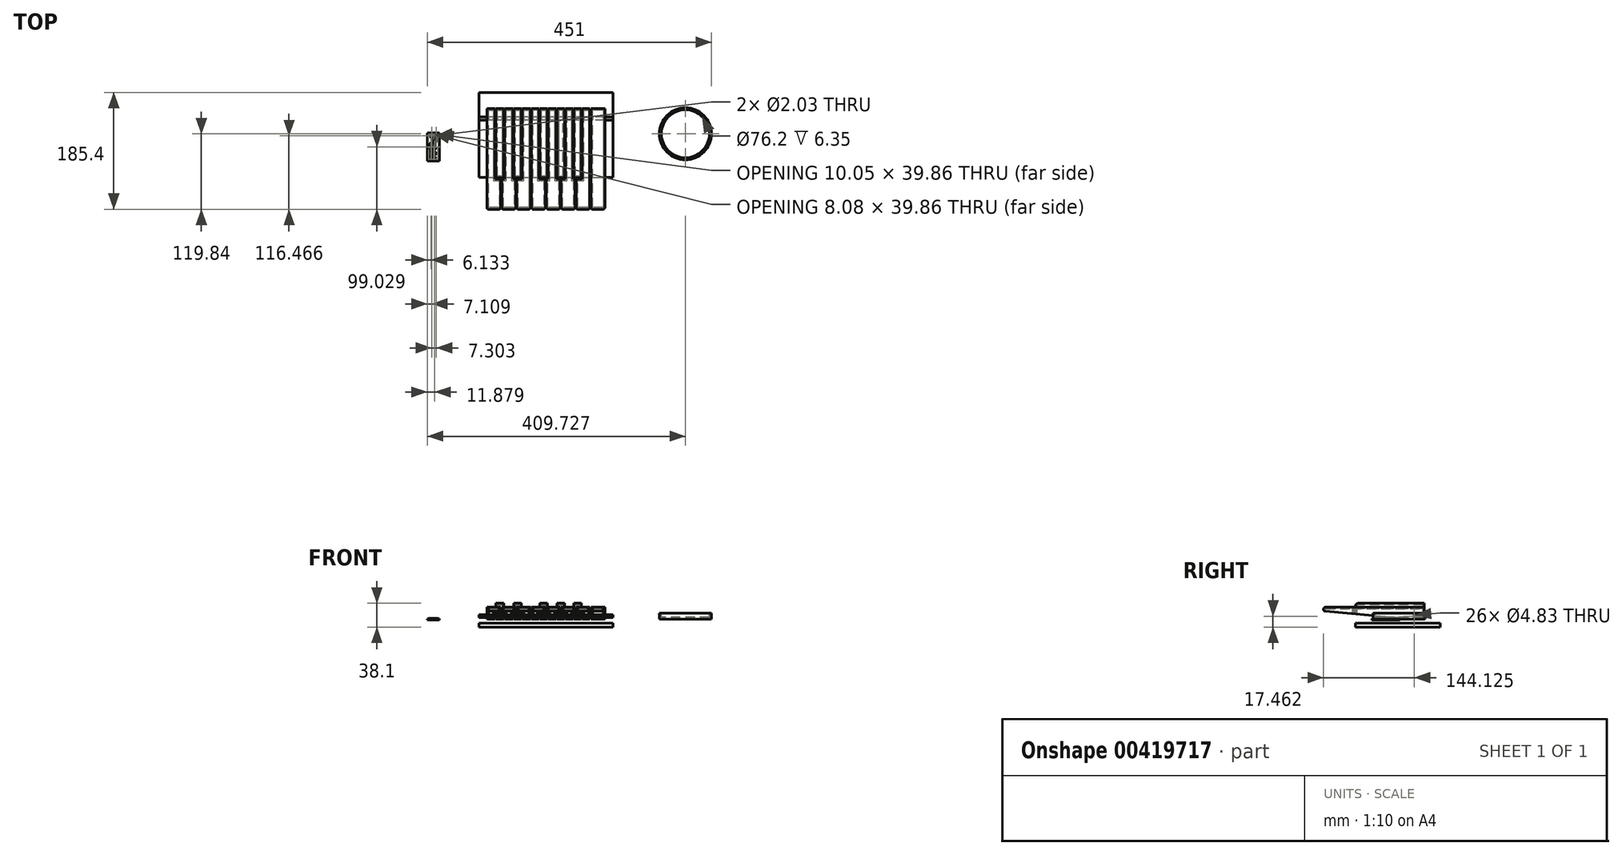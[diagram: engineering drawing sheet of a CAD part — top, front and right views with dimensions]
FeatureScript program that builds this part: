
annotation { "Feature Type Name" : "Feature", "Feature Type Description" : "" }
export const myFeature = defineFeature(function(context is Context, id is Id, definition is map)
    precondition{}
    {
        {
            var Q0;
            Q0=qCreatedBy(makeId("Top.planeOp"),FACE);
            var sketch = newSketch(context, id + "F0", { "sketchPlane" : qUnion([Q0])});
            skLineSegment(sketch, "E0", {"start": v(-10.7, 80) * mm, "end": v(-10.7, -32) * mm});
            skLineSegment(sketch, "E1", {"start": v(-10.7, -32) * mm, "end": v(-0.7, -32) * mm});
            skLineSegment(sketch, "E2", {"start": v(-0.7, -32) * mm, "end": v(-0.7, -80) * mm});
            skLineSegment(sketch, "E3", {"start": v(-0.7, -80) * mm, "end": v(-22.9, -80) * mm});
            skLineSegment(sketch, "E4", {"start": v(-22.9, -80) * mm, "end": v(-22.9, 80) * mm});
            skLineSegment(sketch, "E5", {"start": v(-24.3, 80) * mm, "end": v(-24.3, -80) * mm});
            skLineSegment(sketch, "E6", {"start": v(-24.3, -80) * mm, "end": v(-46.5, -80) * mm});
            skLineSegment(sketch, "E7", {"start": v(-46.5, -80) * mm, "end": v(-46.5, -32) * mm});
            skLineSegment(sketch, "E8", {"start": v(-46.5, -32) * mm, "end": v(-37.5, -32) * mm});
            skLineSegment(sketch, "E9", {"start": v(-37.5, -32) * mm, "end": v(-37.5, 80) * mm});
            skLineSegment(sketch, "E10", {"start": v(-37.5, 80) * mm, "end": v(-24.3, 80) * mm});
            skLineSegment(sketch, "E11", {"start": v(-38.85, 80) * mm, "end": v(-38.85, -30) * mm, "construction": true});
            skLineSegment(sketch, "E12", {"start": v(-38.85, -30) * mm, "end": v(-51.05, -30) * mm, "construction": true});
            skLineSegment(sketch, "E13", {"start": v(-51.05, -30) * mm, "end": v(-51.05, 80) * mm, "construction": true});
            skLineSegment(sketch, "E14", {"start": v(-51.05, 80) * mm, "end": v(-38.85, 80) * mm, "construction": true});
            skLineSegment(sketch, "E15", {"start": v(-52.4, 80) * mm, "end": v(-52.4, -32) * mm});
            skLineSegment(sketch, "E16", {"start": v(-52.4, -32) * mm, "end": v(-47.9, -32) * mm});
            skLineSegment(sketch, "E17", {"start": v(-47.9, -32) * mm, "end": v(-47.9, -80) * mm});
            skLineSegment(sketch, "E18", {"start": v(-47.9, -80) * mm, "end": v(-70.1, -80) * mm});
            skLineSegment(sketch, "E19", {"start": v(-70.1, -80) * mm, "end": v(-70.1, -32) * mm});
            skLineSegment(sketch, "E20", {"start": v(-70.1, -32) * mm, "end": v(-65.6, -32) * mm});
            skLineSegment(sketch, "E21", {"start": v(-65.6, -32) * mm, "end": v(-65.6, 80) * mm});
            skLineSegment(sketch, "E22", {"start": v(-65.6, 80) * mm, "end": v(-52.4, 80) * mm});
            skLineSegment(sketch, "E23", {"start": v(-66.95, 80) * mm, "end": v(-66.95, -30) * mm, "construction": true});
            skLineSegment(sketch, "E24", {"start": v(-66.95, -30) * mm, "end": v(-79.15, -30) * mm, "construction": true});
            skLineSegment(sketch, "E25", {"start": v(-79.15, -30) * mm, "end": v(-79.15, 80) * mm, "construction": true});
            skLineSegment(sketch, "E26", {"start": v(-79.15, 80) * mm, "end": v(-66.95, 80) * mm, "construction": true});
            skLineSegment(sketch, "E27", {"start": v(-80.5, 80) * mm, "end": v(-80.5, -32) * mm});
            skLineSegment(sketch, "E28", {"start": v(-80.5, -32) * mm, "end": v(-71.5, -32) * mm});
            skLineSegment(sketch, "E29", {"start": v(-71.5, -32) * mm, "end": v(-71.5, -80) * mm});
            skLineSegment(sketch, "E30", {"start": v(-71.5, -80) * mm, "end": v(-93.7, -80) * mm});
            skLineSegment(sketch, "E31", {"start": v(-93.7, -80) * mm, "end": v(-93.7, 80) * mm});
            skLineSegment(sketch, "E32", {"start": v(-93.7, 80) * mm, "end": v(-80.5, 80) * mm});
            skLineSegment(sketch, "E33", {"start": v(-9.43, 80) * mm, "end": v(2.77, 80) * mm, "construction": true});
            skLineSegment(sketch, "E34", {"start": v(2.77, 80) * mm, "end": v(2.77, -30) * mm, "construction": true});
            skLineSegment(sketch, "E35", {"start": v(2.77, -30) * mm, "end": v(-9.43, -30) * mm, "construction": true});
            skLineSegment(sketch, "E36", {"start": v(-9.43, -30) * mm, "end": v(-9.43, 80) * mm, "construction": true});
            skLineSegment(sketch, "E37", {"start": v(0.7, -80) * mm, "end": v(0.7, -32) * mm});
            skLineSegment(sketch, "E38", {"start": v(0.7, -32) * mm, "end": v(4.04, -32) * mm});
            skLineSegment(sketch, "E39", {"start": v(4.04, -32) * mm, "end": v(4.04, 80) * mm});
            skLineSegment(sketch, "E40", {"start": v(4.04, 80) * mm, "end": v(16.24, 80) * mm});
            skLineSegment(sketch, "E41", {"start": v(16.24, 80) * mm, "end": v(16.24, -32) * mm});
            skLineSegment(sketch, "E42", {"start": v(16.24, -32) * mm, "end": v(22.9, -32) * mm});
            skLineSegment(sketch, "E43", {"start": v(22.9, -32) * mm, "end": v(22.9, -80) * mm});
            skLineSegment(sketch, "E44", {"start": v(22.9, -80) * mm, "end": v(0.7, -80) * mm});
            skLineSegment(sketch, "E45", {"start": v(24.3, -80) * mm, "end": v(24.3, -32) * mm});
            skLineSegment(sketch, "E46", {"start": v(24.3, -32) * mm, "end": v(30.98, -32) * mm});
            skLineSegment(sketch, "E47", {"start": v(30.98, -32) * mm, "end": v(30.98, 80) * mm});
            skLineSegment(sketch, "E48", {"start": v(30.98, 80) * mm, "end": v(43.18, 80) * mm});
            skLineSegment(sketch, "E49", {"start": v(43.18, 80) * mm, "end": v(43.18, -32) * mm});
            skLineSegment(sketch, "E50", {"start": v(43.18, -32) * mm, "end": v(46.5, -32) * mm});
            skLineSegment(sketch, "E51", {"start": v(46.5, -32) * mm, "end": v(46.5, -80) * mm});
            skLineSegment(sketch, "E52", {"start": v(46.5, -80) * mm, "end": v(24.3, -80) * mm});
            skLineSegment(sketch, "E53", {"start": v(29.7, -30) * mm, "end": v(29.7, 80) * mm, "construction": true});
            skLineSegment(sketch, "E54", {"start": v(29.7, 80) * mm, "end": v(17.5, 80) * mm, "construction": true});
            skLineSegment(sketch, "E55", {"start": v(17.5, 80) * mm, "end": v(17.5, -30) * mm, "construction": true});
            skLineSegment(sketch, "E56", {"start": v(17.5, -30) * mm, "end": v(29.7, -30) * mm, "construction": true});
            skLineSegment(sketch, "E57", {"start": v(70.12, 80) * mm, "end": v(70.12, -80) * mm});
            skLineSegment(sketch, "E58", {"start": v(70.12, -80) * mm, "end": v(47.92, -80) * mm});
            skLineSegment(sketch, "E59", {"start": v(47.92, -80) * mm, "end": v(47.92, -32) * mm});
            skLineSegment(sketch, "E60", {"start": v(47.92, -32) * mm, "end": v(57.92, -32) * mm});
            skLineSegment(sketch, "E61", {"start": v(57.92, -32) * mm, "end": v(57.92, 80) * mm});
            skLineSegment(sketch, "E62", {"start": v(57.92, 80) * mm, "end": v(70.12, 80) * mm});
            skLineSegment(sketch, "E63", {"start": v(56.65, 80) * mm, "end": v(56.65, -30) * mm, "construction": true});
            skLineSegment(sketch, "E64", {"start": v(56.65, -30) * mm, "end": v(44.45, -30) * mm, "construction": true});
            skLineSegment(sketch, "E65", {"start": v(44.45, -30) * mm, "end": v(44.45, 80) * mm, "construction": true});
            skLineSegment(sketch, "E66", {"start": v(44.45, 80) * mm, "end": v(56.65, 80) * mm, "construction": true});
            skLineSegment(sketch, "E67", {"start": v(93.7, 80) * mm, "end": v(93.7, -80) * mm});
            skLineSegment(sketch, "E68", {"start": v(93.7, -80) * mm, "end": v(71.5, -80) * mm});
            skLineSegment(sketch, "E69", {"start": v(71.5, -80) * mm, "end": v(71.5, 80) * mm});
            skLineSegment(sketch, "E70", {"start": v(93.7, 80) * mm, "end": v(71.5, 80) * mm});
            skLineSegment(sketch, "E71", {"start": v(-10.7, 80) * mm, "end": v(-22.9, 80) * mm});
            skSolve(sketch);
        }
        {
            var Q0;
            Q0 = qSketchRegion(id + "F0", true);
            extrude(context, id + "F1", {"entities" : qUnion([Q0]), "depth" : 19.05 * mm});
        }
        {
            var Q0;
            Q0=qCreatedBy(makeId("Top.planeOp"),FACE);
            var sketch = newSketch(context, id + "F2", { "sketchPlane" : qUnion([Q0])});
            skLineSegment(sketch, "E72.13", {"start": v(-38.85, 80) * mm, "end": v(-38.85, -30) * mm});
            skLineSegment(sketch, "E72.14", {"start": v(-38.85, -30) * mm, "end": v(-51.05, -30) * mm});
            skLineSegment(sketch, "E72.15", {"start": v(-51.05, -30) * mm, "end": v(-51.05, 80) * mm});
            skLineSegment(sketch, "E72.16", {"start": v(-51.05, 80) * mm, "end": v(-38.85, 80) * mm});
            skLineSegment(sketch, "E72.25", {"start": v(-66.95, 80) * mm, "end": v(-66.95, -30) * mm});
            skLineSegment(sketch, "E72.26", {"start": v(-66.95, -30) * mm, "end": v(-79.15, -30) * mm});
            skLineSegment(sketch, "E72.27", {"start": v(-79.15, -30) * mm, "end": v(-79.15, 80) * mm});
            skLineSegment(sketch, "E72.28", {"start": v(-79.15, 80) * mm, "end": v(-66.95, 80) * mm});
            skLineSegment(sketch, "E72.35", {"start": v(-9.43, 80) * mm, "end": v(2.77, 80) * mm});
            skLineSegment(sketch, "E72.36", {"start": v(2.77, 80) * mm, "end": v(2.77, -30) * mm});
            skLineSegment(sketch, "E72.37", {"start": v(2.77, -30) * mm, "end": v(-9.43, -30) * mm});
            skLineSegment(sketch, "E72.38", {"start": v(-9.43, -30) * mm, "end": v(-9.43, 80) * mm});
            skLineSegment(sketch, "E72.55", {"start": v(29.7, -30) * mm, "end": v(29.7, 80) * mm});
            skLineSegment(sketch, "E72.56", {"start": v(29.7, 80) * mm, "end": v(17.5, 80) * mm});
            skLineSegment(sketch, "E72.57", {"start": v(17.5, 80) * mm, "end": v(17.5, -30) * mm});
            skLineSegment(sketch, "E72.58", {"start": v(17.5, -30) * mm, "end": v(29.7, -30) * mm});
            skLineSegment(sketch, "E72.65", {"start": v(56.65, 80) * mm, "end": v(56.65, -30) * mm});
            skLineSegment(sketch, "E72.66", {"start": v(56.65, -30) * mm, "end": v(44.45, -30) * mm});
            skLineSegment(sketch, "E72.67", {"start": v(44.45, -30) * mm, "end": v(44.45, 80) * mm});
            skLineSegment(sketch, "E72.68", {"start": v(44.45, 80) * mm, "end": v(56.65, 80) * mm});
            skPoint(sketch, "E72.29.end.orphan", {"position": v(-80.5, -32) * mm});
            skSolve(sketch);
        }
        {
            var Q0;
            Q0 = qSketchRegion(id + "F2", true);
            extrude(context, id + "F3", {"entities" : qUnion([Q0]), "depth" : 25.4 * mm});
        }
        {
            var Q0;
            Q0=makeQuery(id+"F1.opExtrude","SWEPT_FACE",FACE,{"disambiguationData":[OSD([sQuery(id+"F0.wireOp",EDGE,"E31")])]});
            var sketch = newSketch(context, id + "F4", { "sketchPlane" : qUnion([Q0])});
            skCircle(sketch, "E73", {"center": v(-64.12, 4.76) * mm, "radius": 2.41 * mm});
            skSolve(sketch);
        }
        {
            var Q0;
            Q0=makeQuery(id+"F1.opExtrude","SWEPT_FACE",FACE,{"disambiguationData":[OSD([sQuery(id+"F0.wireOp",EDGE,"E31")])]});
            var sketch = newSketch(context, id + "F5", { "sketchPlane" : qUnion([Q0])});
            skLineSegment(sketch, "E74", {"start": v(80, 0) * mm, "end": v(80, 12.7) * mm});
            skCircle(sketch, "E75.0", {"center": v(-64.12, 4.76) * mm, "radius": 2.41 * mm, "construction": true});
            skPoint(sketch, "E76", {"position": v(-64.12, 0) * mm});
            skLineSegment(sketch, "E77", {"start": v(80, 12.7) * mm, "end": v(-64.12, 0) * mm});
            skLineSegment(sketch, "E78", {"start": v(-64.12, 0) * mm, "end": v(80, 0) * mm});
            skSolve(sketch);
        }
        {
            var Q0;
            Q0 = qSketchRegion(id + "F5", true);
            var Q1;
            Q1=makeQuery(id+"F1.opExtrude","SWEPT_FACE",FACE,{"disambiguationData":[OSD([sQuery(id+"F0.wireOp",EDGE,"E67")])]});
            extrude(context, id + "F6", {"entities" : qUnion([Q0]), "operationType" : NewBodyOperationType.REMOVE, "endBound" : BoundingType.THROUGH_ALL, "oppositeDirection" : true, "endBoundEntityFace" : qUnion([Q1]), "depth" : 25.4 * mm});
        }
        {
            var Q0;
            Q0=makeQuery(id+"F1.opExtrude","SWEPT_FACE",FACE,{"disambiguationData":[OSD([sQuery(id+"F0.wireOp",EDGE,"E30")])]});
            var Q1;
            Q1=makeQuery(id+"F1.opExtrude","SWEPT_FACE",FACE,{"disambiguationData":[OSD([sQuery(id+"F0.wireOp",EDGE,"E18")])]});
            var Q2;
            Q2=makeQuery(id+"F1.opExtrude","SWEPT_FACE",FACE,{"disambiguationData":[OSD([sQuery(id+"F0.wireOp",EDGE,"E6")])]});
            var Q3;
            Q3=makeQuery(id+"F1.opExtrude","SWEPT_FACE",FACE,{"disambiguationData":[OSD([sQuery(id+"F0.wireOp",EDGE,"E3")])]});
            var Q4;
            Q4=makeQuery(id+"F1.opExtrude","SWEPT_FACE",FACE,{"disambiguationData":[OSD([sQuery(id+"F0.wireOp",EDGE,"E44")])]});
            var Q5;
            Q5=makeQuery(id+"F1.opExtrude","SWEPT_FACE",FACE,{"disambiguationData":[OSD([sQuery(id+"F0.wireOp",EDGE,"E52")])]});
            var Q6;
            Q6=makeQuery(id+"F1.opExtrude","SWEPT_FACE",FACE,{"disambiguationData":[OSD([sQuery(id+"F0.wireOp",EDGE,"E58")])]});
            var Q7;
            Q7=makeQuery(id+"F1.opExtrude","SWEPT_FACE",FACE,{"disambiguationData":[OSD([sQuery(id+"F0.wireOp",EDGE,"E68")])]});
            fillet(context, id + "F7", {"entities" : qUnion([Q0, Q1, Q2, Q3, Q4, Q5, Q6, Q7]), "radius" : 3.17 * mm, "tangentPropagation" : true, "allowEdgeOverflow" : false});
        }
        {
            var Q0;
            Q0=makeQuery(id+"F1.opExtrude","CAP_FACE",FACE,{"disambiguationData":[OSD([sQuery(id+"F0.wireOp",EDGE,"E27"),sQuery(id+"F0.wireOp",EDGE,"E28"),sQuery(id+"F0.wireOp",EDGE,"E29"),sQuery(id+"F0.wireOp",EDGE,"E30"),sQuery(id+"F0.wireOp",EDGE,"E31"),sQuery(id+"F0.wireOp",EDGE,"E32")])],"isStart":true});
            var Q1;
            {var subQ4=sQuery(id+"F0.wireOp",EDGE,"E27");Q1=makeQuery(id+"F6.boolean.opBoolean","COPY",FACE,{"disambiguationData":[TD([makeQuery(id+"F1.opExtrude","SWEPT_FACE",FACE,{"disambiguationData":[OSD([subQ4])]})])],"derivedFrom":makeQuery(id+"F6.opExtrude","SWEPT_FACE",FACE,{"disambiguationData":[OSD([sQuery(id+"F5.wireOp",EDGE,"E77")])]})});}
            var Q2;
            {var subQ0=sQuery(id+"F2.wireOp",EDGE,"E72.25");Q2=makeQuery(id+"F6.boolean.opBoolean","COPY",FACE,{"disambiguationData":[TD([makeQuery(id+"F3.opExtrude","SWEPT_FACE",FACE,{"disambiguationData":[OSD([subQ0])]})])],"derivedFrom":makeQuery(id+"F6.opExtrude","SWEPT_FACE",FACE,{"disambiguationData":[OSD([sQuery(id+"F5.wireOp",EDGE,"E77")])]})});}
            var Q3;
            {var subQ6=sQuery(id+"F0.wireOp",EDGE,"E15");Q3=makeQuery(id+"F6.boolean.opBoolean","COPY",FACE,{"disambiguationData":[TD([makeQuery(id+"F1.opExtrude","SWEPT_FACE",FACE,{"disambiguationData":[OSD([subQ6])]})])],"derivedFrom":makeQuery(id+"F6.opExtrude","SWEPT_FACE",FACE,{"disambiguationData":[OSD([sQuery(id+"F5.wireOp",EDGE,"E77")])]})});}
            var Q4;
            {var subQ0=sQuery(id+"F2.wireOp",EDGE,"E72.13");Q4=makeQuery(id+"F6.boolean.opBoolean","COPY",FACE,{"disambiguationData":[TD([makeQuery(id+"F3.opExtrude","SWEPT_FACE",FACE,{"disambiguationData":[OSD([subQ0])]})])],"derivedFrom":makeQuery(id+"F6.opExtrude","SWEPT_FACE",FACE,{"disambiguationData":[OSD([sQuery(id+"F5.wireOp",EDGE,"E77")])]})});}
            var Q5;
            {var subQ4=sQuery(id+"F0.wireOp",EDGE,"E5");Q5=makeQuery(id+"F6.boolean.opBoolean","COPY",FACE,{"disambiguationData":[TD([makeQuery(id+"F1.opExtrude","SWEPT_FACE",FACE,{"disambiguationData":[OSD([subQ4])]})])],"derivedFrom":makeQuery(id+"F6.opExtrude","SWEPT_FACE",FACE,{"disambiguationData":[OSD([sQuery(id+"F5.wireOp",EDGE,"E77")])]})});}
            var Q6;
            {var subQ4=sQuery(id+"F0.wireOp",EDGE,"E0");Q6=makeQuery(id+"F6.boolean.opBoolean","COPY",FACE,{"disambiguationData":[TD([makeQuery(id+"F1.opExtrude","SWEPT_FACE",FACE,{"disambiguationData":[OSD([subQ4])]})])],"derivedFrom":makeQuery(id+"F6.opExtrude","SWEPT_FACE",FACE,{"disambiguationData":[OSD([sQuery(id+"F5.wireOp",EDGE,"E77")])]})});}
            var Q7;
            {var subQ6=sQuery(id+"F0.wireOp",EDGE,"E37");Q7=makeQuery(id+"F6.boolean.opBoolean","COPY",FACE,{"disambiguationData":[TD([makeQuery(id+"F1.opExtrude","SWEPT_FACE",FACE,{"disambiguationData":[OSD([subQ6])]})])],"derivedFrom":makeQuery(id+"F6.opExtrude","SWEPT_FACE",FACE,{"disambiguationData":[OSD([sQuery(id+"F5.wireOp",EDGE,"E77")])]})});}
            var Q8;
            {var subQ2=sQuery(id+"F2.wireOp",EDGE,"E72.36");Q8=makeQuery(id+"F6.boolean.opBoolean","COPY",FACE,{"disambiguationData":[TD([makeQuery(id+"F3.opExtrude","SWEPT_FACE",FACE,{"disambiguationData":[OSD([subQ2])]})])],"derivedFrom":makeQuery(id+"F6.opExtrude","SWEPT_FACE",FACE,{"disambiguationData":[OSD([sQuery(id+"F5.wireOp",EDGE,"E77")])]})});}
            var Q9;
            {var subQ0=sQuery(id+"F2.wireOp",EDGE,"E72.55");Q9=makeQuery(id+"F6.boolean.opBoolean","COPY",FACE,{"disambiguationData":[TD([makeQuery(id+"F3.opExtrude","SWEPT_FACE",FACE,{"disambiguationData":[OSD([subQ0])]})])],"derivedFrom":makeQuery(id+"F6.opExtrude","SWEPT_FACE",FACE,{"disambiguationData":[OSD([sQuery(id+"F5.wireOp",EDGE,"E77")])]})});}
            var Q10;
            {var subQ6=sQuery(id+"F0.wireOp",EDGE,"E45");Q10=makeQuery(id+"F6.boolean.opBoolean","COPY",FACE,{"disambiguationData":[TD([makeQuery(id+"F1.opExtrude","SWEPT_FACE",FACE,{"disambiguationData":[OSD([subQ6])]})])],"derivedFrom":makeQuery(id+"F6.opExtrude","SWEPT_FACE",FACE,{"disambiguationData":[OSD([sQuery(id+"F5.wireOp",EDGE,"E77")])]})});}
            var Q11;
            {var subQ0=sQuery(id+"F2.wireOp",EDGE,"E72.65");Q11=makeQuery(id+"F6.boolean.opBoolean","COPY",FACE,{"disambiguationData":[TD([makeQuery(id+"F3.opExtrude","SWEPT_FACE",FACE,{"disambiguationData":[OSD([subQ0])]})])],"derivedFrom":makeQuery(id+"F6.opExtrude","SWEPT_FACE",FACE,{"disambiguationData":[OSD([sQuery(id+"F5.wireOp",EDGE,"E77")])]})});}
            var Q12;
            {var subQ4=sQuery(id+"F0.wireOp",EDGE,"E57");Q12=makeQuery(id+"F6.boolean.opBoolean","COPY",FACE,{"disambiguationData":[TD([makeQuery(id+"F1.opExtrude","SWEPT_FACE",FACE,{"disambiguationData":[OSD([subQ4])]})])],"derivedFrom":makeQuery(id+"F6.opExtrude","SWEPT_FACE",FACE,{"disambiguationData":[OSD([sQuery(id+"F5.wireOp",EDGE,"E77")])]})});}
            var Q13;
            {var subQ0=sQuery(id+"F0.wireOp",EDGE,"E67");Q13=makeQuery(id+"F6.boolean.opBoolean","COPY",FACE,{"disambiguationData":[TD([makeQuery(id+"F1.opExtrude","SWEPT_FACE",FACE,{"disambiguationData":[OSD([subQ0])]})])],"derivedFrom":makeQuery(id+"F6.opExtrude","SWEPT_FACE",FACE,{"disambiguationData":[OSD([sQuery(id+"F5.wireOp",EDGE,"E77")])]})});}
            var Q14;
            Q14=makeQuery(id+"F1.opExtrude","CAP_FACE",FACE,{"disambiguationData":[OSD([sQuery(id+"F0.wireOp",EDGE,"E67"),sQuery(id+"F0.wireOp",EDGE,"E68"),sQuery(id+"F0.wireOp",EDGE,"E69"),sQuery(id+"F0.wireOp",EDGE,"E70")])],"isStart":true});
            var Q15;
            Q15=makeQuery(id+"F1.opExtrude","CAP_FACE",FACE,{"disambiguationData":[OSD([sQuery(id+"F0.wireOp",EDGE,"E57"),sQuery(id+"F0.wireOp",EDGE,"E58"),sQuery(id+"F0.wireOp",EDGE,"E59"),sQuery(id+"F0.wireOp",EDGE,"E60"),sQuery(id+"F0.wireOp",EDGE,"E61"),sQuery(id+"F0.wireOp",EDGE,"E62")])],"isStart":true});
            var Q16;
            Q16=makeQuery(id+"F3.opExtrude","CAP_FACE",FACE,{"disambiguationData":[OSD([sQuery(id+"F2.wireOp",EDGE,"E72.65"),sQuery(id+"F2.wireOp",EDGE,"E72.66"),sQuery(id+"F2.wireOp",EDGE,"E72.67"),sQuery(id+"F2.wireOp",EDGE,"E72.68")])],"isStart":true});
            var Q17;
            Q17=makeQuery(id+"F1.opExtrude","CAP_FACE",FACE,{"disambiguationData":[OSD([sQuery(id+"F0.wireOp",EDGE,"E45"),sQuery(id+"F0.wireOp",EDGE,"E46"),sQuery(id+"F0.wireOp",EDGE,"E47"),sQuery(id+"F0.wireOp",EDGE,"E48"),sQuery(id+"F0.wireOp",EDGE,"E49"),sQuery(id+"F0.wireOp",EDGE,"E50"),sQuery(id+"F0.wireOp",EDGE,"E51"),sQuery(id+"F0.wireOp",EDGE,"E52")])],"isStart":true});
            var Q18;
            Q18=makeQuery(id+"F3.opExtrude","CAP_FACE",FACE,{"disambiguationData":[OSD([sQuery(id+"F2.wireOp",EDGE,"E72.55"),sQuery(id+"F2.wireOp",EDGE,"E72.56"),sQuery(id+"F2.wireOp",EDGE,"E72.57"),sQuery(id+"F2.wireOp",EDGE,"E72.58")])],"isStart":true});
            var Q19;
            Q19=makeQuery(id+"F1.opExtrude","CAP_FACE",FACE,{"disambiguationData":[OSD([sQuery(id+"F0.wireOp",EDGE,"E37"),sQuery(id+"F0.wireOp",EDGE,"E38"),sQuery(id+"F0.wireOp",EDGE,"E39"),sQuery(id+"F0.wireOp",EDGE,"E40"),sQuery(id+"F0.wireOp",EDGE,"E41"),sQuery(id+"F0.wireOp",EDGE,"E42"),sQuery(id+"F0.wireOp",EDGE,"E43"),sQuery(id+"F0.wireOp",EDGE,"E44")])],"isStart":true});
            var Q20;
            Q20=makeQuery(id+"F3.opExtrude","CAP_FACE",FACE,{"disambiguationData":[OSD([sQuery(id+"F2.wireOp",EDGE,"E72.35"),sQuery(id+"F2.wireOp",EDGE,"E72.36"),sQuery(id+"F2.wireOp",EDGE,"E72.37"),sQuery(id+"F2.wireOp",EDGE,"E72.38")])],"isStart":true});
            var Q21;
            Q21=makeQuery(id+"F1.opExtrude","CAP_FACE",FACE,{"disambiguationData":[OSD([sQuery(id+"F0.wireOp",EDGE,"E0"),sQuery(id+"F0.wireOp",EDGE,"E1"),sQuery(id+"F0.wireOp",EDGE,"E2"),sQuery(id+"F0.wireOp",EDGE,"E3"),sQuery(id+"F0.wireOp",EDGE,"E4"),sQuery(id+"F0.wireOp",EDGE,"E71")])],"isStart":true});
            var Q22;
            Q22=makeQuery(id+"F1.opExtrude","CAP_FACE",FACE,{"disambiguationData":[OSD([sQuery(id+"F0.wireOp",EDGE,"E5"),sQuery(id+"F0.wireOp",EDGE,"E6"),sQuery(id+"F0.wireOp",EDGE,"E7"),sQuery(id+"F0.wireOp",EDGE,"E8"),sQuery(id+"F0.wireOp",EDGE,"E9"),sQuery(id+"F0.wireOp",EDGE,"E10")])],"isStart":true});
            var Q23;
            Q23=makeQuery(id+"F3.opExtrude","CAP_FACE",FACE,{"disambiguationData":[OSD([sQuery(id+"F2.wireOp",EDGE,"E72.13"),sQuery(id+"F2.wireOp",EDGE,"E72.14"),sQuery(id+"F2.wireOp",EDGE,"E72.15"),sQuery(id+"F2.wireOp",EDGE,"E72.16")])],"isStart":true});
            var Q24;
            Q24=makeQuery(id+"F1.opExtrude","CAP_FACE",FACE,{"disambiguationData":[OSD([sQuery(id+"F0.wireOp",EDGE,"E15"),sQuery(id+"F0.wireOp",EDGE,"E16"),sQuery(id+"F0.wireOp",EDGE,"E17"),sQuery(id+"F0.wireOp",EDGE,"E18"),sQuery(id+"F0.wireOp",EDGE,"E19"),sQuery(id+"F0.wireOp",EDGE,"E20"),sQuery(id+"F0.wireOp",EDGE,"E21"),sQuery(id+"F0.wireOp",EDGE,"E22")])],"isStart":true});
            var Q25;
            Q25=makeQuery(id+"F3.opExtrude","CAP_FACE",FACE,{"disambiguationData":[OSD([sQuery(id+"F2.wireOp",EDGE,"E72.25"),sQuery(id+"F2.wireOp",EDGE,"E72.26"),sQuery(id+"F2.wireOp",EDGE,"E72.27"),sQuery(id+"F2.wireOp",EDGE,"E72.28")])],"isStart":true});
            shell(context, id + "F8", {"entities" : qUnion([Q0, Q1, Q2, Q3, Q4, Q5, Q6, Q7, Q8, Q9, Q10, Q11, Q12, Q13, Q14, Q15, Q16, Q17, Q18, Q19, Q20, Q21, Q22, Q23, Q24, Q25]), "thickness" : 2.54 * mm});
        }
        {
            var Q0;
            Q0 = qSketchRegion(id + "F4", true);
            extrude(context, id + "F9", {"entities" : qUnion([Q0]), "operationType" : NewBodyOperationType.REMOVE, "endBound" : BoundingType.THROUGH_ALL, "oppositeDirection" : true, "depth" : 25.4 * mm});
        }
        {
            var Q0;
            Q0=makeQuery(id+"F3.opExtrude","CAP_EDGE",EDGE,{"disambiguationData":[OSD([sQuery(id+"F2.wireOp",EDGE,"E72.26")])],"isStart":false});
            var Q1;
            Q1=makeQuery(id+"F3.opExtrude","CAP_EDGE",EDGE,{"disambiguationData":[OSD([sQuery(id+"F2.wireOp",EDGE,"E72.14")])],"isStart":false});
            var Q2;
            Q2=makeQuery(id+"F3.opExtrude","CAP_EDGE",EDGE,{"disambiguationData":[OSD([sQuery(id+"F2.wireOp",EDGE,"E72.37")])],"isStart":false});
            var Q3;
            Q3=makeQuery(id+"F3.opExtrude","CAP_EDGE",EDGE,{"disambiguationData":[OSD([sQuery(id+"F2.wireOp",EDGE,"E72.58")])],"isStart":false});
            var Q4;
            Q4=makeQuery(id+"F3.opExtrude","CAP_EDGE",EDGE,{"disambiguationData":[OSD([sQuery(id+"F2.wireOp",EDGE,"E72.66")])],"isStart":false});
            fillet(context, id + "F10", {"entities" : qUnion([Q0, Q1, Q2, Q3, Q4]), "radius" : 6.35 * mm, "tangentPropagation" : true, "allowEdgeOverflow" : false});
        }
        {
            var Q0;
            Q0=makeQuery(id+"F1.opExtrude","SWEPT_FACE",FACE,{"disambiguationData":[OSD([sQuery(id+"F0.wireOp",EDGE,"E31")])]});
            cPlane(context, id + "F11", {"entities" : qUnion([Q0]), "cplaneType" : CPlaneType.OFFSET, "offset" : 12.7 * mm, "width" : 152.4 * mm, "height" : 152.4 * mm});
        }
        {
            var Q0;
            Q0=qCreatedBy(id+"F11.planeOp",FACE);
            var sketch = newSketch(context, id + "F12", { "sketchPlane" : qUnion([Q0])});
            skCircle(sketch, "E79.0", {"center": v(-64.12, 4.76) * mm, "radius": 2.41 * mm});
            skSolve(sketch);
        }
        {
            var Q0;
            Q0=makeQuery(id+"F1.opExtrude","SWEPT_FACE",FACE,{"disambiguationData":[OSD([sQuery(id+"F0.wireOp",EDGE,"E67")])]});
            cPlane(context, id + "F13", {"entities" : qUnion([Q0]), "cplaneType" : CPlaneType.OFFSET, "offset" : 12.7 * mm, "width" : 152.4 * mm, "height" : 152.4 * mm});
        }
        {
            var Q0;
            Q0 = qSketchRegion(id + "F12", true);
            var Q1;
            Q1=qCreatedBy(id+"F13.planeOp",FACE);
            extrude(context, id + "F14", {"entities" : qUnion([Q0]), "endBound" : BoundingType.UP_TO_SURFACE, "oppositeDirection" : true, "endBoundEntityFace" : qUnion([Q1]), "depth" : 25.4 * mm});
        }
        {
            var Q0;
            Q0=qCreatedBy(makeId("Top.planeOp"),FACE);
            cPlane(context, id + "F15", {"entities" : qUnion([Q0]), "cplaneType" : CPlaneType.OFFSET, "offset" : 6.35 * mm, "oppositeDirection" : true, "width" : 152.4 * mm, "height" : 152.4 * mm});
        }
        {
            var Q0;
            Q0=qCreatedBy(id+"F15.planeOp",FACE);
            var sketch = newSketch(context, id + "F16", { "sketchPlane" : qUnion([Q0])});
            skLineSegment(sketch, "E80", {"start": v(-106.4, 66.54) * mm, "end": v(106.4, 66.54) * mm, "construction": true});
            skLineSegment(sketch, "E81", {"start": v(106.4, 61.71) * mm, "end": v(-106.4, 61.71) * mm, "construction": true});
            skLineSegment(sketch, "E82.bottom", {"start": v(-106.4, 105.4) * mm, "end": v(106.4, 105.4) * mm});
            skLineSegment(sketch, "E82.top", {"start": v(-106.4, -29.2) * mm, "end": v(106.4, -29.2) * mm});
            skLineSegment(sketch, "E82.left", {"start": v(-106.4, 105.4) * mm, "end": v(-106.4, -29.2) * mm});
            skLineSegment(sketch, "E82.right", {"start": v(106.4, 105.4) * mm, "end": v(106.4, -29.2) * mm});
            skLineSegment(sketch, "E83.0", {"start": v(-74.67, -80) * mm, "end": v(-90.52, -80) * mm, "construction": true});
            skPoint(sketch, "E84.0", {"position": v(-87.1, 80) * mm});
            skSolve(sketch);
        }
        {
            var Q0;
            Q0 = qSketchRegion(id + "F16", true);
            extrude(context, id + "F17", {"entities" : qUnion([Q0]), "oppositeDirection" : true, "depth" : 6.35 * mm});
        }
        {
            var Q0;
            Q0=qCreatedBy(makeId("Top.planeOp"),FACE);
            var sketch = newSketch(context, id + "F18", { "sketchPlane" : qUnion([Q0])});
            skLineSegment(sketch, "E85", {"start": v(-179.87, 0) * mm, "end": v(-184.36, 4.5) * mm});
            skLineSegment(sketch, "E86", {"start": v(-184.36, 4.5) * mm, "end": v(-179.87, 8.98) * mm});
            skLineSegment(sketch, "E87", {"start": v(-179.87, 8.98) * mm, "end": v(-184.36, 13.47) * mm});
            skLineSegment(sketch, "E88", {"start": v(-184.36, 13.47) * mm, "end": v(-179.87, 17.96) * mm});
            skLineSegment(sketch, "E89", {"start": v(-179.87, 17.96) * mm, "end": v(-184.36, 22.45) * mm});
            skLineSegment(sketch, "E90", {"start": v(-184.36, 22.45) * mm, "end": v(-179.87, 26.94) * mm});
            skLineSegment(sketch, "E91", {"start": v(-179.87, 26.94) * mm, "end": v(-179.87, 33.3) * mm});
            skLineSegment(sketch, "E92", {"start": v(-179.6, 4.5) * mm, "end": v(-175.1, 8.98) * mm});
            skLineSegment(sketch, "E93", {"start": v(-175.1, 8.98) * mm, "end": v(-179.6, 13.47) * mm});
            skLineSegment(sketch, "E94", {"start": v(-179.6, 13.47) * mm, "end": v(-175.1, 17.96) * mm});
            skLineSegment(sketch, "E95", {"start": v(-175.1, 17.96) * mm, "end": v(-179.6, 22.45) * mm});
            skLineSegment(sketch, "E96", {"start": v(-179.6, 22.45) * mm, "end": v(-175.1, 26.94) * mm});
            skLineSegment(sketch, "E97", {"start": v(-175.1, 26.94) * mm, "end": v(-175.1, 33.3) * mm});
            skLineSegment(sketch, "E98", {"start": v(-179.6, 4.5) * mm, "end": v(-175.1, 0) * mm});
            skSolve(sketch);
        }
        {
            var Q0;
            Q0=qCreatedBy(makeId("Front.planeOp"),FACE);
            var Q1;
            Q1=sQuery(id+"F18.wireOp",VERTEX,"E91.end");
            cPlane(context, id + "F19", {"entities" : qUnion([Q0, Q1]), "cplaneType" : CPlaneType.PLANE_POINT, "offset" : 25.4 * mm, "width" : 152.4 * mm, "height" : 152.4 * mm});
        }
        {
            var Q0;
            Q0=qCreatedBy(id+"F19.planeOp",FACE);
            var sketch = newSketch(context, id + "F20", { "sketchPlane" : qUnion([Q0])});
            skLineSegment(sketch, "E99.bottom", {"start": v(-181.14, 1.27) * mm, "end": v(-178.6, 1.27) * mm});
            skLineSegment(sketch, "E99.top", {"start": v(-181.14, -1.27) * mm, "end": v(-178.6, -1.27) * mm});
            skLineSegment(sketch, "E99.left", {"start": v(-181.14, 1.27) * mm, "end": v(-181.14, -1.27) * mm});
            skLineSegment(sketch, "E99.right", {"start": v(-178.6, 1.27) * mm, "end": v(-178.6, -1.27) * mm});
            skPoint(sketch, "E100", {"position": v(-179.87, 0) * mm});
            skPoint(sketch, "E100.positionSnap0", {"position": v(-181.14, 0) * mm});
            skPoint(sketch, "E100.positionSnap1", {"position": v(-179.87, 1.27) * mm});
            skLineSegment(sketch, "E101.bottom", {"start": v(-176.38, 1.27) * mm, "end": v(-173.84, 1.27) * mm});
            skLineSegment(sketch, "E101.top", {"start": v(-176.38, -1.27) * mm, "end": v(-173.84, -1.27) * mm});
            skLineSegment(sketch, "E101.left", {"start": v(-176.38, 1.27) * mm, "end": v(-176.38, -1.27) * mm});
            skLineSegment(sketch, "E101.right", {"start": v(-173.84, 1.27) * mm, "end": v(-173.84, -1.27) * mm});
            skPoint(sketch, "E102", {"position": v(-175.1, 0) * mm});
            skPoint(sketch, "E102.positionSnap0", {"position": v(-176.38, 0) * mm});
            skPoint(sketch, "E102.positionSnap1", {"position": v(-175.1, 1.27) * mm});
            skSolve(sketch);
        }
        {
            var Q0;
            Q0=makeQuery(id+"F20.imprint","IMPRINT",FACE,{"disambiguationData":[TD([[makeQuery(id+"F20.imprint","IMPRINT",EDGE,{"derivedFrom":sQuery(id+"F20.wireOp",EDGE,"E99.bottom")}),-1.0]])]});
            var Q1;
            Q1=sQuery(id+"F18.wireOp",EDGE,"E91");
            var Q2;
            Q2=sQuery(id+"F18.wireOp",EDGE,"E90");
            var Q3;
            Q3=sQuery(id+"F18.wireOp",EDGE,"E89");
            var Q4;
            Q4=sQuery(id+"F18.wireOp",EDGE,"E88");
            var Q5;
            Q5=sQuery(id+"F18.wireOp",EDGE,"E87");
            var Q6;
            Q6=sQuery(id+"F18.wireOp",EDGE,"E86");
            var Q7;
            Q7=sQuery(id+"F18.wireOp",EDGE,"E85");
            sweep(context, id + "F21", {"profiles" : qUnion([Q0]), "path" : qUnion([Q1, Q2, Q3, Q4, Q5, Q6, Q7])});
        }
        {
            var Q0;
            Q0=makeQuery(id+"F20.imprint","IMPRINT",FACE,{"disambiguationData":[TD([[makeQuery(id+"F20.imprint","IMPRINT",EDGE,{"derivedFrom":sQuery(id+"F20.wireOp",EDGE,"E101.bottom")}),-1.0]])]});
            var Q1;
            Q1=sQuery(id+"F18.wireOp",EDGE,"E97");
            var Q2;
            Q2=sQuery(id+"F18.wireOp",EDGE,"E96");
            var Q3;
            Q3=sQuery(id+"F18.wireOp",EDGE,"E95");
            var Q4;
            Q4=sQuery(id+"F18.wireOp",EDGE,"E94");
            var Q5;
            Q5=sQuery(id+"F18.wireOp",EDGE,"E93");
            var Q6;
            Q6=sQuery(id+"F18.wireOp",EDGE,"E92");
            var Q7;
            Q7=sQuery(id+"F18.wireOp",EDGE,"E98");
            sweep(context, id + "F22", {"operationType" : NewBodyOperationType.ADD, "profiles" : qUnion([Q0]), "path" : qUnion([Q1, Q2, Q3, Q4, Q5, Q6, Q7])});
        }
        {
            var Q0;
            Q0=makeQuery(id+"F22.opSweep","SWEPT_FACE",FACE,{"disambiguationData":[OSD([sQuery(id+"F18.wireOp",EDGE,"E97"),sQuery(id+"F20.wireOp",EDGE,"E101.bottom")])]});
            var sketch = newSketch(context, id + "F23", { "sketchPlane" : qUnion([Q0])});
            skCircle(sketch, "E103", {"center": v(-173.84, 36.47) * mm, "radius": 1.02 * mm});
            skPoint(sketch, "E104", {"position": v(-176.38, 33.3) * mm});
            skArc(sketch, "E105", {"start": v(-173.84, 33.93) * mm, "mid": v(-172.04, 38.26) * mm, "end": v(-176.38, 36.47) * mm});
            skLineSegment(sketch, "E106", {"start": v(-176.38, 33.3) * mm, "end": v(-176.38, 36.47) * mm});
            skLineSegment(sketch, "E107", {"start": v(-173.84, 33.3) * mm, "end": v(-173.84, 33.93) * mm});
            skPoint(sketch, "E108.0", {"position": v(-178.6, 33.3) * mm});
            skLineSegment(sketch, "E109", {"start": v(-178.6, 33.3) * mm, "end": v(-176.38, 33.3) * mm, "construction": true});
            skLineSegment(sketch, "E110", {"start": v(-176.38, 33.3) * mm, "end": v(-173.84, 33.3) * mm});
            skPoint(sketch, "E111", {"position": v(-177.5, 33.3) * mm});
            skLineSegment(sketch, "E112", {"start": v(-177.5, 33.3) * mm, "end": v(-177.5, 39.2) * mm, "construction": true});
            skCircle(sketch, "E113.MirrorC", {"center": v(-181.14, 36.47) * mm, "radius": 1.02 * mm});
            skArc(sketch, "E114.MirrorCS", {"start": v(-181.14, 33.93) * mm, "mid": v(-182.94, 38.26) * mm, "end": v(-178.6, 36.47) * mm});
            skLineSegment(sketch, "E115.MirrorCS", {"start": v(-178.6, 33.3) * mm, "end": v(-178.6, 36.47) * mm});
            skLineSegment(sketch, "E116.MirrorCS", {"start": v(-178.6, 33.3) * mm, "end": v(-181.14, 33.3) * mm});
            skLineSegment(sketch, "E117.MirrorCS", {"start": v(-181.14, 33.3) * mm, "end": v(-181.14, 33.93) * mm});
            skSolve(sketch);
        }
        {
            var Q0;
            Q0 = qSketchRegion(id + "F23", true);
            var Q1;
            Q1=makeQuery(id+"F22.opSweep","SWEPT_FACE",FACE,{"disambiguationData":[OSD([sQuery(id+"F18.wireOp",EDGE,"E97"),sQuery(id+"F20.wireOp",EDGE,"E101.top")])]});
            extrude(context, id + "F24", {"entities" : qUnion([Q0]), "endBound" : BoundingType.UP_TO_SURFACE, "oppositeDirection" : true, "endBoundEntityFace" : qUnion([Q1]), "depth" : 25.4 * mm});
        }
        {
            var Q0;
            Q0=makeQuery(id+"F21.opSweep","SWEPT_FACE",FACE,{"disambiguationData":[OSD([sQuery(id+"F18.wireOp",EDGE,"E91"),sQuery(id+"F20.wireOp",EDGE,"E99.top")])]});
            var sketch = newSketch(context, id + "F25", { "sketchPlane" : qUnion([Q0])});
            skLineSegment(sketch, "E118.0.0", {"start": v(-181.14, -33.3) * mm, "end": v(-181.14, -27.47) * mm});
            skLineSegment(sketch, "E118.0.1", {"start": v(-181.14, -27.47) * mm, "end": v(-186.16, -22.45) * mm});
            skLineSegment(sketch, "E118.0.2", {"start": v(-186.16, -22.45) * mm, "end": v(-181.67, -17.96) * mm});
            skLineSegment(sketch, "E118.0.3", {"start": v(-181.67, -17.96) * mm, "end": v(-186.16, -13.47) * mm});
            skLineSegment(sketch, "E118.0.4", {"start": v(-186.16, -13.47) * mm, "end": v(-181.67, -8.98) * mm});
            skLineSegment(sketch, "E118.0.5", {"start": v(-181.67, -8.98) * mm, "end": v(-186.16, -4.5) * mm});
            skLineSegment(sketch, "E118.0.6", {"start": v(-186.16, -4.5) * mm, "end": v(-180.77, 0.9) * mm});
            skLineSegment(sketch, "E118.0.7", {"start": v(-178.97, -0.9) * mm, "end": v(-180.77, 0.9) * mm});
            skLineSegment(sketch, "E118.0.8", {"start": v(-178.97, -0.9) * mm, "end": v(-182.57, -4.5) * mm});
            skLineSegment(sketch, "E118.0.9", {"start": v(-182.57, -4.5) * mm, "end": v(-178.08, -8.98) * mm});
            skLineSegment(sketch, "E118.0.10", {"start": v(-178.08, -8.98) * mm, "end": v(-182.57, -13.47) * mm});
            skLineSegment(sketch, "E118.0.11", {"start": v(-182.57, -13.47) * mm, "end": v(-178.08, -17.96) * mm});
            skLineSegment(sketch, "E118.0.12", {"start": v(-178.08, -17.96) * mm, "end": v(-182.57, -22.45) * mm});
            skLineSegment(sketch, "E118.0.13", {"start": v(-182.57, -22.45) * mm, "end": v(-178.6, -26.41) * mm});
            skLineSegment(sketch, "E118.0.14", {"start": v(-178.6, -26.41) * mm, "end": v(-178.6, -33.3) * mm});
            skLineSegment(sketch, "E119.0.0", {"start": v(-176.38, -33.3) * mm, "end": v(-176.38, -27.47) * mm});
            skLineSegment(sketch, "E119.0.1", {"start": v(-176.38, -27.47) * mm, "end": v(-181.4, -22.45) * mm});
            skLineSegment(sketch, "E119.0.2", {"start": v(-181.4, -22.45) * mm, "end": v(-176.9, -17.96) * mm});
            skLineSegment(sketch, "E119.0.3", {"start": v(-176.9, -17.96) * mm, "end": v(-181.4, -13.47) * mm});
            skLineSegment(sketch, "E119.0.4", {"start": v(-181.4, -13.47) * mm, "end": v(-176.9, -8.98) * mm});
            skLineSegment(sketch, "E119.0.5", {"start": v(-176.9, -8.98) * mm, "end": v(-181.4, -4.5) * mm});
            skLineSegment(sketch, "E119.0.6", {"start": v(-181.4, -4.5) * mm, "end": v(-176, 0.9) * mm});
            skLineSegment(sketch, "E119.0.7", {"start": v(-174.21, -0.9) * mm, "end": v(-176, 0.9) * mm});
            skLineSegment(sketch, "E119.0.8", {"start": v(-174.21, -0.9) * mm, "end": v(-177.8, -4.5) * mm});
            skLineSegment(sketch, "E119.0.9", {"start": v(-177.8, -4.5) * mm, "end": v(-173.31, -8.98) * mm});
            skLineSegment(sketch, "E119.0.10", {"start": v(-173.31, -8.98) * mm, "end": v(-177.8, -13.47) * mm});
            skLineSegment(sketch, "E119.0.11", {"start": v(-177.8, -13.47) * mm, "end": v(-173.31, -17.96) * mm});
            skLineSegment(sketch, "E119.0.12", {"start": v(-173.31, -17.96) * mm, "end": v(-177.8, -22.45) * mm});
            skLineSegment(sketch, "E119.0.13", {"start": v(-177.8, -22.45) * mm, "end": v(-173.84, -26.41) * mm});
            skLineSegment(sketch, "E119.0.14", {"start": v(-173.84, -26.41) * mm, "end": v(-173.84, -33.3) * mm});
            skLineSegment(sketch, "E120.0.0", {"start": v(-181.14, -33.93) * mm, "end": v(-181.14, -33.3) * mm});
            skLineSegment(sketch, "E120.0.2", {"start": v(-178.6, -33.3) * mm, "end": v(-178.6, -36.47) * mm});
            skArc(sketch, "E120.0.3", {"start": v(-178.6, -36.47) * mm, "mid": v(-182.94, -38.26) * mm, "end": v(-181.14, -33.93) * mm});
            skLineSegment(sketch, "E121.0.1", {"start": v(-173.84, -33.3) * mm, "end": v(-173.84, -33.93) * mm});
            skArc(sketch, "E121.0.2", {"start": v(-173.84, -33.93) * mm, "mid": v(-172.04, -38.26) * mm, "end": v(-176.38, -36.47) * mm});
            skLineSegment(sketch, "E121.0.3", {"start": v(-176.38, -36.47) * mm, "end": v(-176.38, -33.3) * mm});
            skPoint(sketch, "E122", {"position": v(-181.05, -39) * mm});
            skPoint(sketch, "E123", {"position": v(-181.14, -39) * mm});
            skPoint(sketch, "E124", {"position": v(-171.3, -36.47) * mm});
            skLineSegment(sketch, "E125.bottom", {"start": v(-171.3, -39) * mm, "end": v(-186.16, -39) * mm, "construction": true});
            skLineSegment(sketch, "E125.top", {"start": v(-171.3, 0.9) * mm, "end": v(-186.16, 0.9) * mm, "construction": true});
            skLineSegment(sketch, "E125.left", {"start": v(-171.3, 0.9) * mm, "end": v(-171.3, -39) * mm, "construction": true});
            skLineSegment(sketch, "E125.right", {"start": v(-186.16, 0.9) * mm, "end": v(-186.16, -39) * mm, "construction": true});
            skLineSegment(sketch, "E126", {"start": v(-171.3, -19.05) * mm, "end": v(-186.16, -19.05) * mm, "construction": true});
            skLineSegment(sketch, "E127", {"start": v(-178.73, 0.9) * mm, "end": v(-178.73, -39) * mm, "construction": true});
            skLineSegment(sketch, "E128.bottom", {"start": v(-188.25, 3.17) * mm, "end": v(-169.2, 3.17) * mm});
            skLineSegment(sketch, "E128.top", {"start": v(-188.25, -41.28) * mm, "end": v(-169.2, -41.28) * mm});
            skLineSegment(sketch, "E128.left", {"start": v(-188.25, 3.17) * mm, "end": v(-188.25, -41.28) * mm});
            skLineSegment(sketch, "E128.right", {"start": v(-169.2, 3.17) * mm, "end": v(-169.2, -41.28) * mm});
            skPoint(sketch, "E129", {"position": v(-178.73, -19.05) * mm});
            skPoint(sketch, "E129.positionSnap0", {"position": v(-169.2, -19.05) * mm});
            skPoint(sketch, "E129.positionSnap1", {"position": v(-178.73, 3.17) * mm});
            skSolve(sketch);
        }
        {
            var Q0;
            Q0 = qSketchRegion(id + "F25", true);
            extrude(context, id + "F26", {"entities" : qUnion([Q0]), "oppositeDirection" : true, "depth" : 2.03 * mm});
        }
        {
            var Q0;
            Q0=qCreatedBy(makeId("Top.planeOp"),FACE);
            var sketch = newSketch(context, id + "F27", { "sketchPlane" : qUnion([Q0])});
            skCircle(sketch, "E130", {"center": v(221.48, 39.84) * mm, "radius": 41.28 * mm});
            skSolve(sketch);
        }
        {
            var Q0;
            Q0=makeQuery(id+"F27.imprint","IMPRINT",FACE,{"disambiguationData":[TD([[makeQuery(id+"F27.imprint","IMPRINT",EDGE,{"derivedFrom":sQuery(id+"F27.wireOp",EDGE,"E130")}),1.0]])]});
            extrude(context, id + "F28", {"entities" : qUnion([Q0]), "depth" : 9.52 * mm});
        }
        {
            var Q0;
            Q0=makeQuery(id+"F28.opExtrude","CAP_FACE",FACE,{"disambiguationData":[OSD([sQuery(id+"F27.wireOp",EDGE,"E130")])],"isStart":false});
            var sketch = newSketch(context, id + "F29", { "sketchPlane" : qUnion([Q0])});
            skCircle(sketch, "E131.0", {"center": v(221.48, 39.84) * mm, "radius": 41.28 * mm, "construction": true});
            skCircle(sketch, "E132", {"center": v(221.48, 39.84) * mm, "radius": 38.1 * mm});
            skSolve(sketch);
        }
        {
            var Q0;
            Q0 = qSketchRegion(id + "F29", true);
            extrude(context, id + "F30", {"entities" : qUnion([Q0]), "operationType" : NewBodyOperationType.REMOVE, "oppositeDirection" : true, "depth" : 6.35 * mm});
        }
    });
